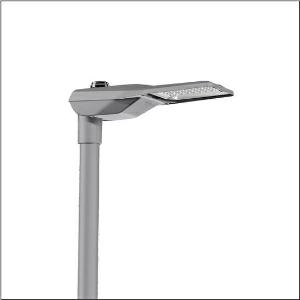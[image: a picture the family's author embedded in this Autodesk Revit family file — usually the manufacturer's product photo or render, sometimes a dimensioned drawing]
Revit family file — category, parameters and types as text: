
# Revit family: streetlight_sl_21_mini___stw1_0a_5xe6e47n08gb_debc
name_source: partatom
category: Lighting Fixtures
units: mm (PartAtom-declared; Revit-internal decimal feet)

## family parameters
Cut with Voids When Loaded = No
Host = Face
Light Source = No
Part Type = Normal
Room Calculation Point = No
Round Connector Dimension = Use Diameter
Shared = No

## types (1)
- --- (1 x LED, 6180 lm, 40.4 W, 4000K)
    Apparent Load = 40 VA
    CIE Flux Codes = 38 75 98 100 100
    Color Rendering = 70
    Color Temperature = 4000K
    Default Elevation = 1800 mm
    Description = Streetlight SL 21 mini, mast luminaire, primary light control with lens, of PMMA, primary optical cover: cover, of toughened safety glass, transparent, light distribution: STW1.0a, light emission: direct distribution, primary light characteristic: asymmetric, installation type: side-entry, LED, 3G 1.5mm², High Power LED, rated luminous flux: 6.180lm, luminous efficacy: 153lm/W, light colour: 740, colour temperature: 4000K, control: overheat protection, pre-setting: linear dimming characteristic, constant luminous flux control, time-dependent luminous flux control, flexible luminous flux parameterisation, mains connection: 230..240V, AC, 50/60Hz, connection cable pre-assembled, cable length: 8,5m, wiring characteristics: H07RN-F, start of lifetime: 40W, end of service life: 41W, reduction: 19W, luminaire housing, of diecast aluminium (EN AC-44300), powder-coated, Siteco® metallic grey (DB 702S), corrosivity category C5 mid according to DIN EN ISO 12944, multi-level sealing system, sealing non-destructively replaceable, inclination adjustable: 0°, 5°, 10°, 15°, length: 628mm, width: 235mm, height: 110mm, spigot size: 42mm (side-entry), protection rating (complete): IP66, insulation class (complete): insulation class I (protective earthing), certification: CE, ENEC, ENEC+, VDE, impact resistance: IK09, permissible operating ambient temperature for outdoor applications: -40..+50°C, standard-compliant lighting for roads and squares, packaging unit: 1 piece

Light Distribution: STW1.0a
    Height = 110 mm
    Lamp = 1 x LED
    Lamp Light Flux = 6180 lm
    Lamp Power = 40.4 W
    Lamp count = 1
    Length = 625 mm
    Luminous efficacy = 153 lm/W
    Manufacturer = Siteco
    ModVariant = No
    Model = 5XE6E47N08GB
    Number of Poles = 1
    OnlyDefault = Yes
    Power Factor = 1
    Product Name = Streetlight SL 21 mini | STW1.0a
    Product group = mast luminaire | pylon top
    ProductGroupID = 6100
    Protection Class = Protection class I
    Protection Degree = IP 66
    RLX_Detail_Level = 1
    RLX_Emergency_Light_Flux = 0 lm
    RLX_Emergency_Type = 0
    RLX_Emergency_Type_DB = No
    RlxData = <blob elided: 91833 chars, md5=3eb54028>
    Socket = socket
    Standby Power = 0 W
    System Light Flux = 6180 lm
    System Power = 40 W
    Type Comments = factory setting: luminous flux: 100 % | dim-lin: 254 | 812 mA
    Type Image = l_1294379.jpg
    URL = http://relux.com
    VarID = @adj_105441
    Voltage = 0 V
    Weight = 0.00 kg
    Width = 234 mm

## geometry (parser evidence)
native form markers: Blend x4, Sweep x10
no freeform markers — native parametric forms only
